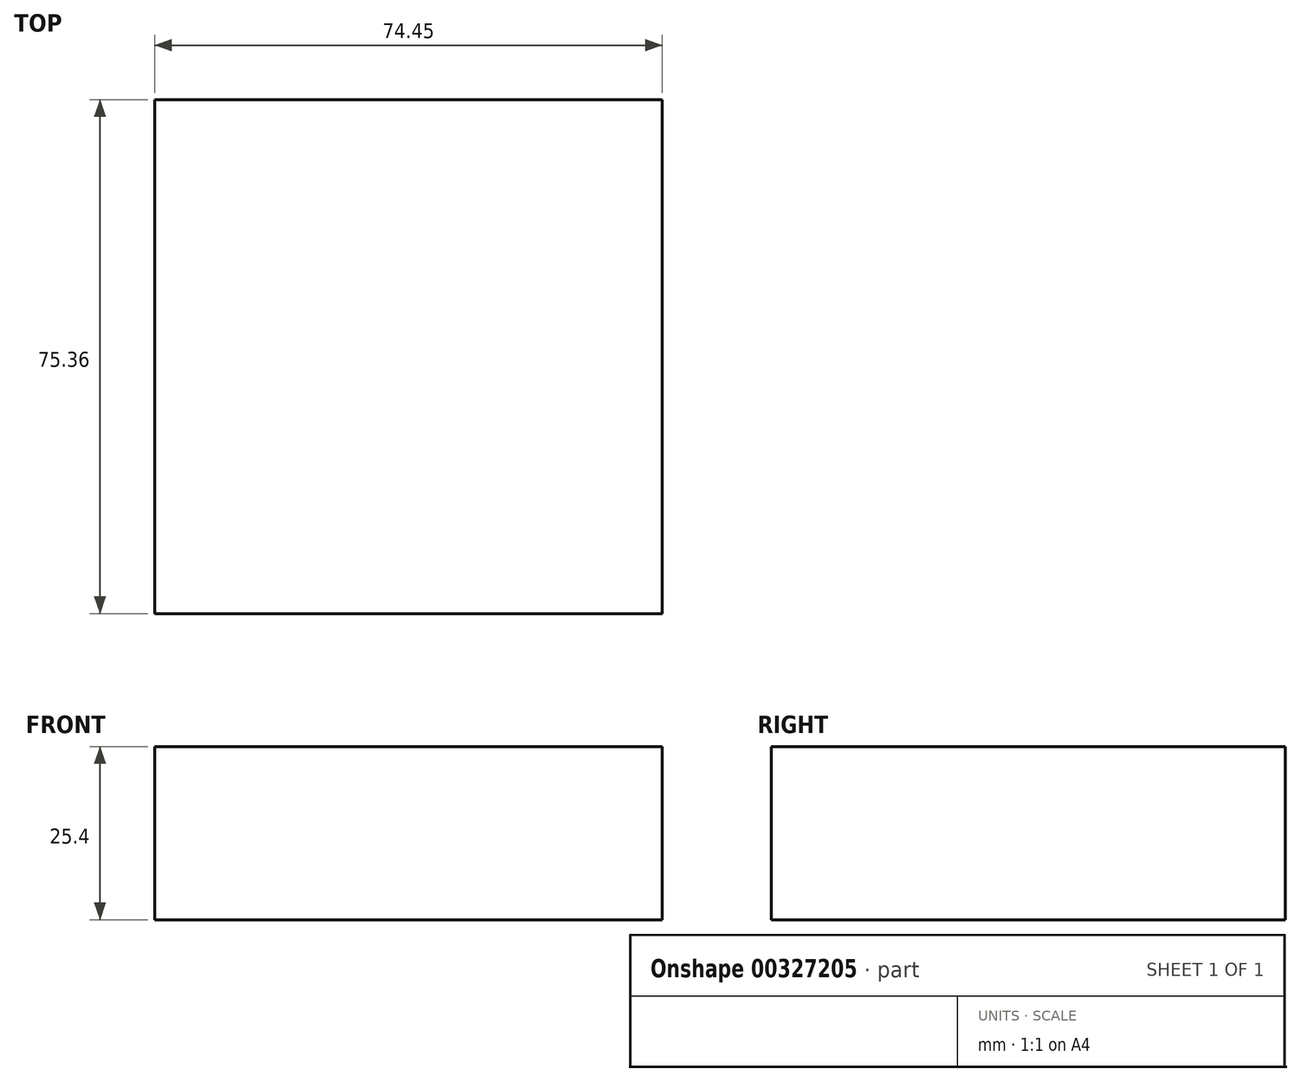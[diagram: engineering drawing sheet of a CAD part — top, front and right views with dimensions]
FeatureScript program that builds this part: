
annotation { "Feature Type Name" : "Feature", "Feature Type Description" : "" }
export const myFeature = defineFeature(function(context is Context, id is Id, definition is map)
    precondition{}
    {
        {
            var Q0;
            Q0=qCreatedBy(makeId("Top.planeOp"),FACE);
            var sketch = newSketch(context, id + "F0", { "sketchPlane" : qUnion([Q0])});
            skLineSegment(sketch, "E0.bottom", {"start": v(74.45, 75.36) * mm, "end": v(0, 75.36) * mm});
            skLineSegment(sketch, "E0.top", {"start": v(74.45, 0) * mm, "end": v(0, 0) * mm});
            skLineSegment(sketch, "E0.left", {"start": v(74.45, 75.36) * mm, "end": v(74.45, 0) * mm});
            skLineSegment(sketch, "E0.right", {"start": v(0, 75.36) * mm, "end": v(0, 0) * mm});
            skSolve(sketch);
        }
        {
            var Q0;
            Q0=makeQuery(id+"F0.imprint","IMPRINT",FACE,{"disambiguationData":[TD([[makeQuery(id+"F0.imprint","IMPRINT",EDGE,{"derivedFrom":sQuery(id+"F0.wireOp",EDGE,"E0.bottom")}),1.0]])]});
            extrude(context, id + "F1", {"entities" : qUnion([Q0]), "depth" : 25.4 * mm});
        }
    });
